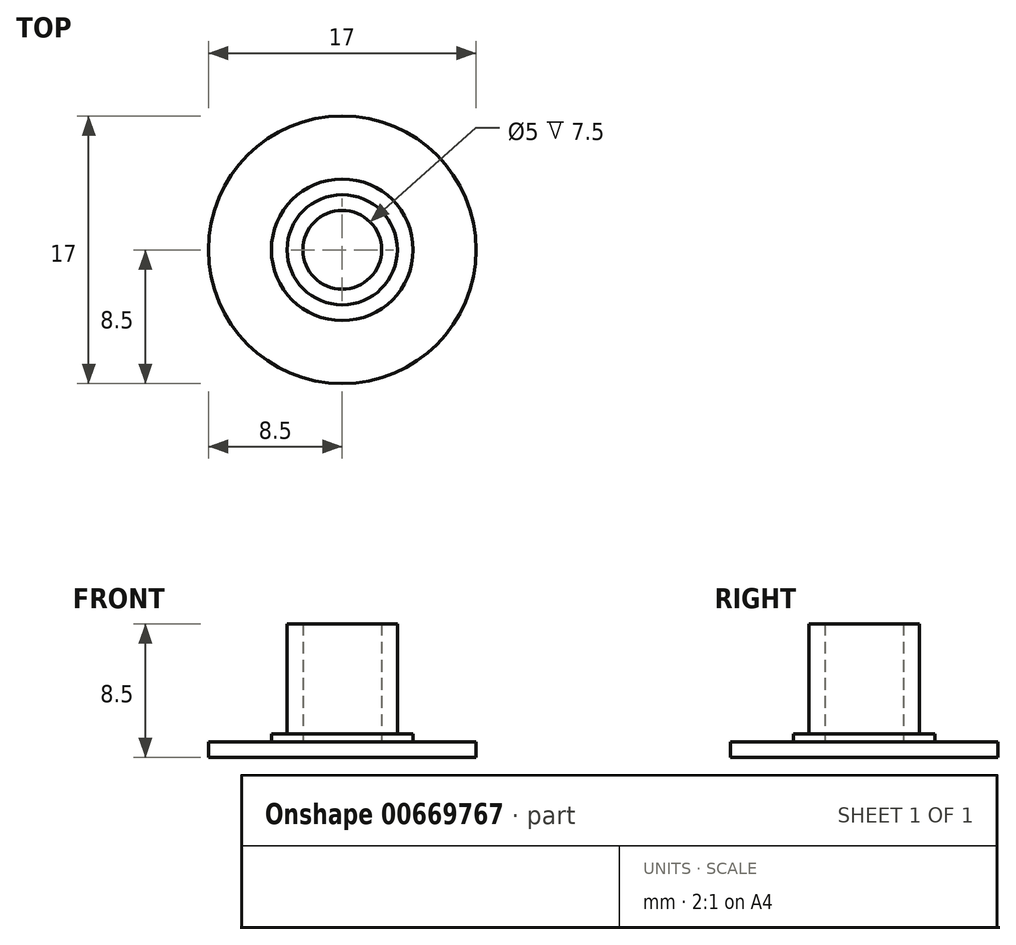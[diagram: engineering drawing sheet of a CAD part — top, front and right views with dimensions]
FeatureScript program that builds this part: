
annotation { "Feature Type Name" : "Feature", "Feature Type Description" : "" }
export const myFeature = defineFeature(function(context is Context, id is Id, definition is map)
    precondition{}
    {
        {
            var Q0;
            Q0=qCreatedBy(makeId("Front.planeOp"),FACE);
            var sketch = newSketch(context, id + "F0", { "sketchPlane" : qUnion([Q0])});
            skLineSegment(sketch, "E0", {"start": v(0, 0) * mm, "end": v(0, 13.14) * mm, "construction": true});
            skLineSegment(sketch, "E1", {"start": v(0, 0) * mm, "end": v(-8.5, 0) * mm});
            skLineSegment(sketch, "E2", {"start": v(-8.5, 0) * mm, "end": v(-8.5, 1) * mm});
            skLineSegment(sketch, "E3", {"start": v(-8.5, 1) * mm, "end": v(-4.5, 1) * mm});
            skLineSegment(sketch, "E4", {"start": v(-3.5, 1.5) * mm, "end": v(-3.5, 8.5) * mm});
            skLineSegment(sketch, "E5", {"start": v(-3.5, 8.5) * mm, "end": v(-2.5, 8.5) * mm});
            skLineSegment(sketch, "E6", {"start": v(-2.5, 8.5) * mm, "end": v(-2.5, 1) * mm});
            skLineSegment(sketch, "E7", {"start": v(-2.5, 1) * mm, "end": v(0, 1) * mm});
            skLineSegment(sketch, "E8", {"start": v(0, 1) * mm, "end": v(0, 0) * mm});
            skLineSegment(sketch, "E9", {"start": v(-4.5, 1) * mm, "end": v(-4.5, 1.5) * mm});
            skLineSegment(sketch, "E10", {"start": v(-4.5, 1.5) * mm, "end": v(-3.5, 1.5) * mm});
            skSolve(sketch);
        }
        {
            var Q0;
            Q0 = qSketchRegion(id + "F0", true);
            var Q1;
            Q1=sQuery(id+"F0.wireOp",EDGE,"E0");
            revolve(context, id + "F1", {"entities" : qUnion([Q0]), "axis" : qUnion([Q1]), "revolveType" : RevolveType.FULL});
        }
    });
